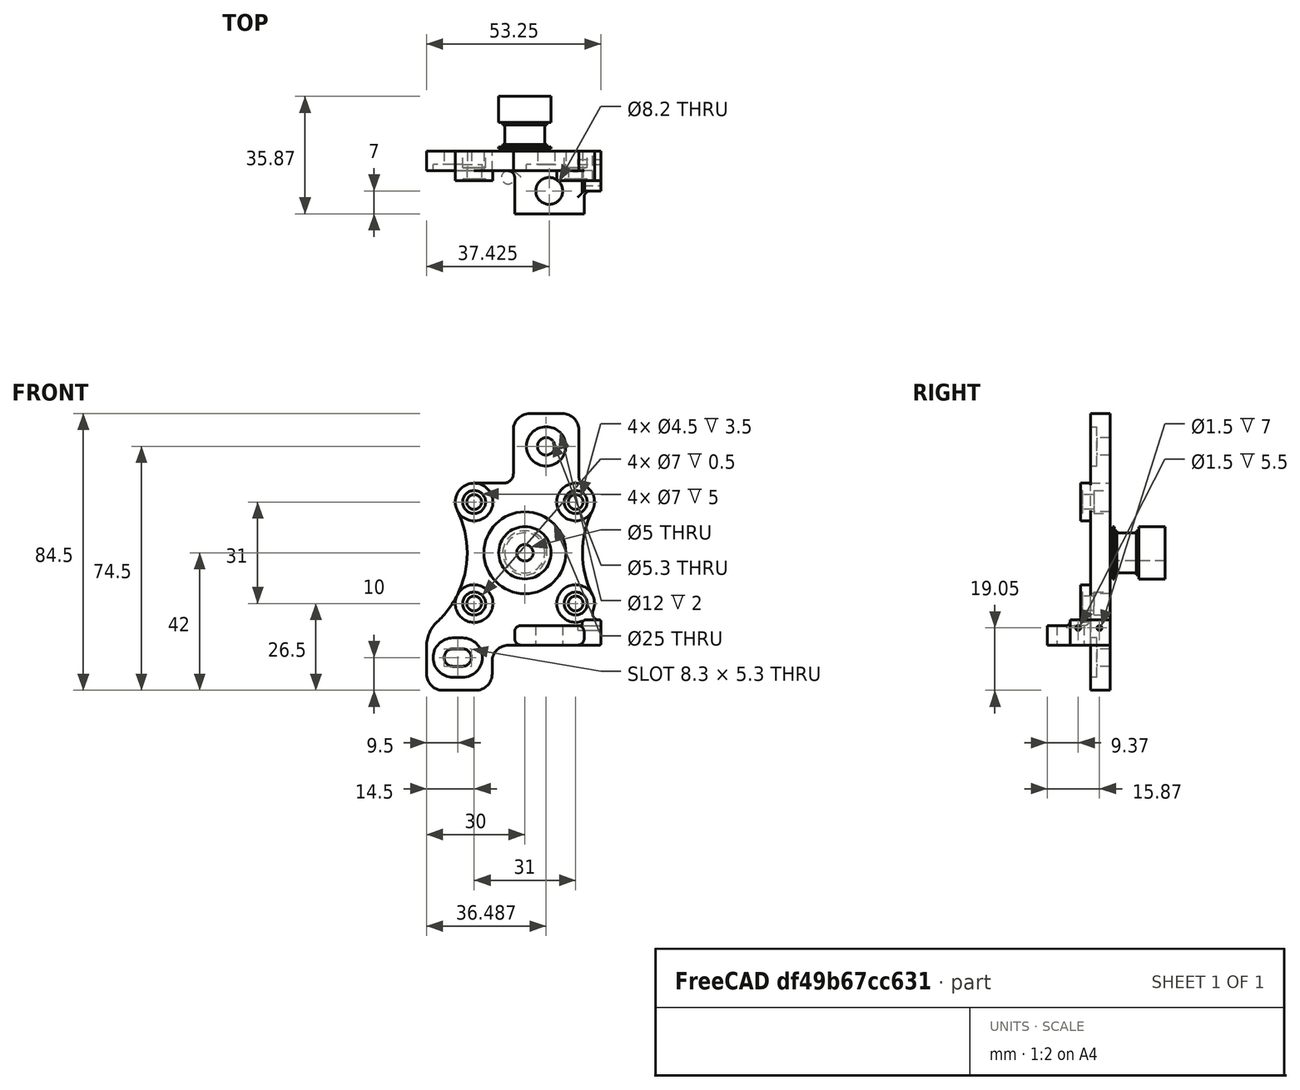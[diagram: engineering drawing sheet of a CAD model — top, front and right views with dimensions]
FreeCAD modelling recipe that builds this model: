
FCSTD DOCUMENT  (FreeCAD 0.17R10423 (Git))
Label: org_motor_z
License: All rights reserved
LicenseURL: http://en.wikipedia.org/wiki/All_rights_reserved
objects: Part::Compound×3, Part::Feature×2
note: 5 computed .brp shape members not serialized (recipe doc carries the construction recipe); baked Part::Feature solids carry a one-line shape summary decoded from their .brp

FEATURE [Part::Feature] Part__Feature028  label="GT2 20t Pulley v1 (1) (1)"
  Placement = pos=(-25,398.75,392.5) rot=(0.707107,0,-0.707107;3.14159rad)
  shape: bbox 16 x 16 x 16 mm, 12 faces (baked)
FEATURE [Part::Compound] COMPOUND001  label="COMPOUND033"
FEATURE [Part::Compound] A_Motor_v1__1___1_
  Links = -> [Part__Feature028,COMPOUND001]
FEATURE [Part::Feature] Part__Feature031  label="SOLID001"
  Placement = pos=(-226.675,292.876,245.5) rot=(0.57735,0.57735,-0.57735;2.0944rad)
  shape: bbox 53.25 x 19.12 x 84.5 mm, 93 faces (baked)
FEATURE [Part::Compound] A_Motor_Mount
  Links = -> [A_Motor_v1__1___1_,Part__Feature031]
